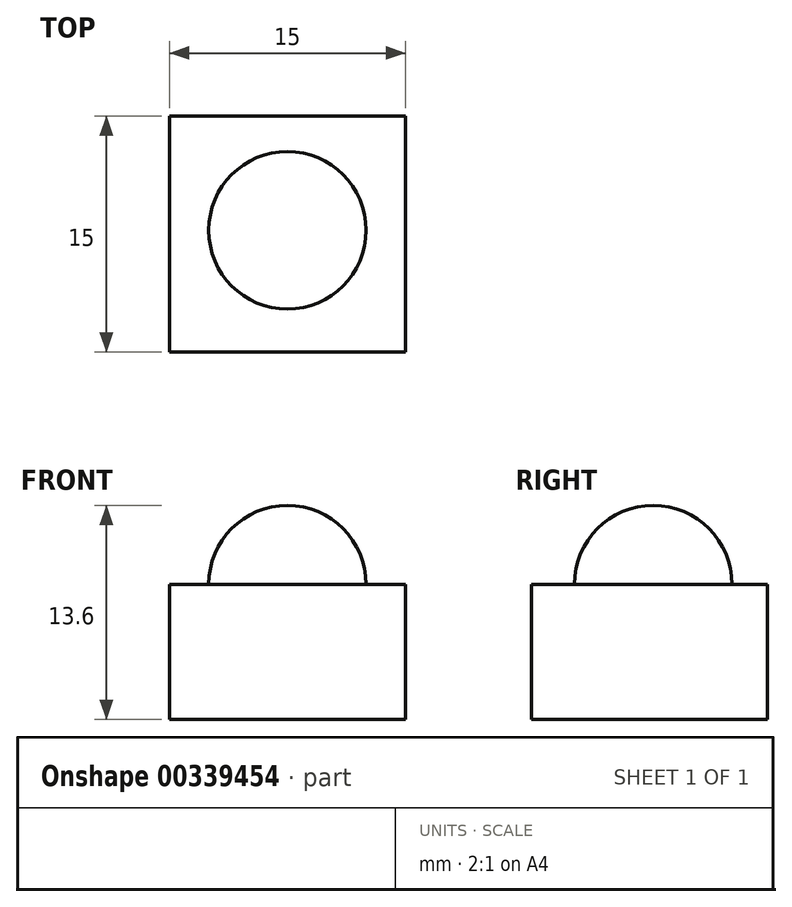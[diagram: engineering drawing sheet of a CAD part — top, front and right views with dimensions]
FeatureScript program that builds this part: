
annotation { "Feature Type Name" : "Feature", "Feature Type Description" : "" }
export const myFeature = defineFeature(function(context is Context, id is Id, definition is map)
    precondition{}
    {
        {
            var Q0;
            Q0=qCreatedBy(makeId("Top.planeOp"),FACE);
            var sketch = newSketch(context, id + "F0", { "sketchPlane" : qUnion([Q0])});
            skLineSegment(sketch, "E0.bottom", {"start": v(-15, 21.02) * mm, "end": v(0, 21.02) * mm});
            skLineSegment(sketch, "E0.top", {"start": v(-15, 6.02) * mm, "end": v(0, 6.02) * mm});
            skLineSegment(sketch, "E0.left", {"start": v(-15, 21.02) * mm, "end": v(-15, 6.02) * mm});
            skLineSegment(sketch, "E0.right", {"start": v(0, 21.02) * mm, "end": v(0, 6.02) * mm});
            skSolve(sketch);
        }
        {
            var Q0;
            Q0=qSketchRegion(id+"F0",true);
            extrude(context, id + "F1", {"entities" : qUnion([Q0]), "depth" : 8.6 * mm});
        }
        {
            var Q0;
            Q0=makeQuery(id+"F1.opExtrude","CAP_FACE",FACE,{"disambiguationData":[OSD([sQuery(id+"F0.wireOp",EDGE,"E0.bottom"),sQuery(id+"F0.wireOp",EDGE,"E0.top"),sQuery(id+"F0.wireOp",EDGE,"E0.left"),sQuery(id+"F0.wireOp",EDGE,"E0.right")])],"isStart":false});
            var sketch = newSketch(context, id + "F2", { "sketchPlane" : qUnion([Q0])});
            skArc(sketch, "E1", {"start": v(-7.5, 18.75) * mm, "mid": v(-12.5, 13.75) * mm, "end": v(-7.5, 8.75) * mm});
            skPoint(sketch, "E1.centerSnap0", {"position": v(-7.5, 21.02) * mm});
            skLineSegment(sketch, "E2", {"start": v(-7.5, 18.75) * mm, "end": v(-7.5, 8.75) * mm});
            skSolve(sketch);
        }
        {
            var Q0;
            Q0=makeQuery(id+"F2.imprint","IMPRINT",FACE,{"disambiguationData":[TD([[makeQuery(id+"F2.imprint","IMPRINT",EDGE,{"derivedFrom":sQuery(id+"F2.wireOp",EDGE,"E1")}),1.0]])]});
            var Q1;
            Q1=sQuery(id+"F2.wireOp",EDGE,"E2");
            revolve(context, id + "F3", {"operationType" : NewBodyOperationType.ADD, "entities" : qUnion([Q0]), "axis" : qUnion([Q1]), "revolveType" : RevolveType.FULL, "oppositeDirection" : true});
        }
    });
